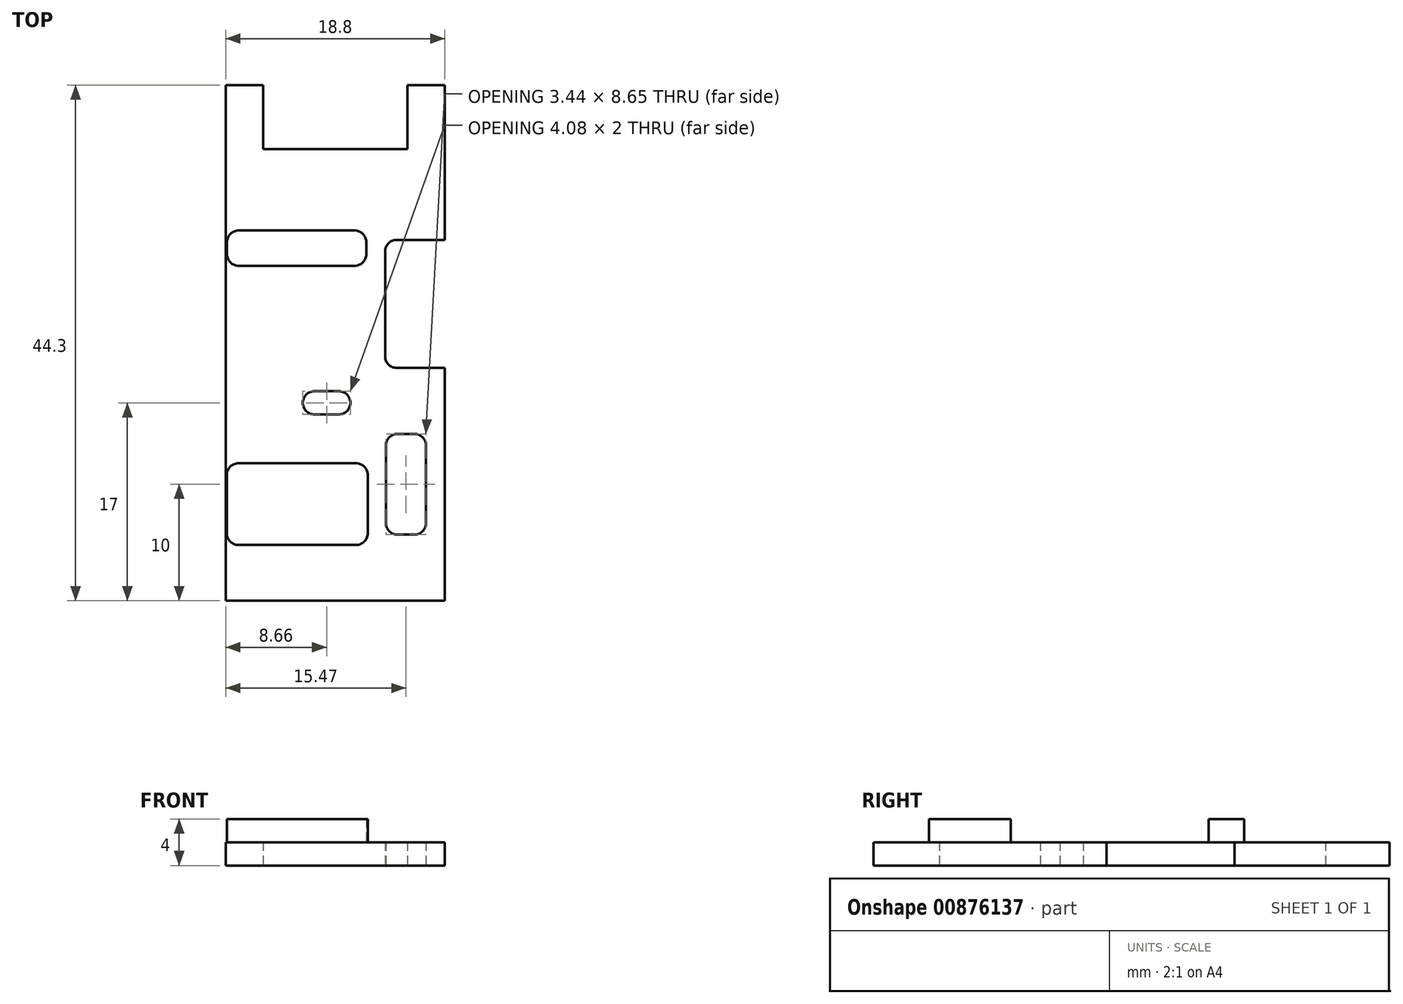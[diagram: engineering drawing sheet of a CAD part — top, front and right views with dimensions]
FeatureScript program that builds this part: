
annotation { "Feature Type Name" : "Feature", "Feature Type Description" : "" }
export const myFeature = defineFeature(function(context is Context, id is Id, definition is map)
    precondition{}
    {
        {
            var Q0;
            Q0=qCreatedBy(makeId("Top.planeOp"),FACE);
            var sketch = newSketch(context, id + "F0", { "sketchPlane" : qUnion([Q0])});
            skLineSegment(sketch, "E0", {"start": v(9.4, 22.15) * mm, "end": v(6.2, 22.15) * mm});
            skLineSegment(sketch, "E1", {"start": v(6.2, 16.65) * mm, "end": v(-6.2, 16.65) * mm});
            skLineSegment(sketch, "E2", {"start": v(-6.2, 22.15) * mm, "end": v(-9.4, 22.15) * mm});
            skLineSegment(sketch, "E3", {"start": v(-9.4, 22.15) * mm, "end": v(-9.4, -22.15) * mm});
            skLineSegment(sketch, "E4", {"start": v(-9.4, -22.15) * mm, "end": v(9.4, -22.15) * mm});
            skLineSegment(sketch, "E5", {"start": v(4.28, -1.15) * mm, "end": v(4.28, 7.85) * mm});
            skPoint(sketch, "E6.visualSharp", {"position": v(4.28, 8.85) * mm});
            skArc(sketch, "E6.filletArc", {"start": v(5.28, 8.85) * mm, "mid": v(4.57, 8.56) * mm, "end": v(4.28, 7.85) * mm});
            skPoint(sketch, "E7.visualSharp", {"position": v(4.28, -2.15) * mm});
            skArc(sketch, "E7.filletArc", {"start": v(4.28, -1.15) * mm, "mid": v(4.57, -1.86) * mm, "end": v(5.28, -2.15) * mm});
            skLineSegment(sketch, "E8.bottom", {"start": v(5.35, -7.82) * mm, "end": v(6.8, -7.82) * mm});
            skLineSegment(sketch, "E8.top", {"start": v(5.35, -16.48) * mm, "end": v(6.8, -16.48) * mm});
            skLineSegment(sketch, "E8.left", {"start": v(4.35, -8.82) * mm, "end": v(4.35, -15.48) * mm});
            skLineSegment(sketch, "E8.right", {"start": v(7.8, -8.82) * mm, "end": v(7.8, -15.48) * mm});
            skLineSegment(sketch, "E9.bottom", {"start": v(-1.78, -4.15) * mm, "end": v(0.3, -4.15) * mm});
            skLineSegment(sketch, "E9.top", {"start": v(-1.78, -6.15) * mm, "end": v(0.3, -6.15) * mm});
            skLineSegment(sketch, "E9.left", {"start": v(-2.78, -5.15) * mm, "end": v(-2.78, -5.15) * mm});
            skLineSegment(sketch, "E9.right", {"start": v(1.3, -5.15) * mm, "end": v(1.3, -5.15) * mm});
            skPoint(sketch, "E10.visualSharp", {"position": v(4.35, -7.82) * mm});
            skArc(sketch, "E10.filletArc", {"start": v(5.35, -7.82) * mm, "mid": v(4.64, -8.12) * mm, "end": v(4.35, -8.82) * mm});
            skPoint(sketch, "E11.visualSharp", {"position": v(7.8, -7.82) * mm});
            skArc(sketch, "E11.filletArc", {"start": v(7.8, -8.82) * mm, "mid": v(7.5, -8.12) * mm, "end": v(6.8, -7.82) * mm});
            skPoint(sketch, "E12.visualSharp", {"position": v(4.35, -16.48) * mm});
            skArc(sketch, "E12.filletArc", {"start": v(4.35, -15.48) * mm, "mid": v(4.64, -16.18) * mm, "end": v(5.35, -16.48) * mm});
            skPoint(sketch, "E13.visualSharp", {"position": v(7.8, -16.48) * mm});
            skArc(sketch, "E13.filletArc", {"start": v(6.8, -16.48) * mm, "mid": v(7.5, -16.18) * mm, "end": v(7.8, -15.48) * mm});
            skPoint(sketch, "E14.visualSharp", {"position": v(-2.78, -4.15) * mm});
            skArc(sketch, "E14.filletArc", {"start": v(-1.78, -4.15) * mm, "mid": v(-2.49, -4.44) * mm, "end": v(-2.78, -5.15) * mm});
            skPoint(sketch, "E15.visualSharp", {"position": v(1.3, -4.15) * mm});
            skArc(sketch, "E15.filletArc", {"start": v(1.3, -5.15) * mm, "mid": v(1, -4.44) * mm, "end": v(0.3, -4.15) * mm});
            skPoint(sketch, "E16.visualSharp", {"position": v(1.3, -6.15) * mm});
            skArc(sketch, "E16.filletArc", {"start": v(0.3, -6.15) * mm, "mid": v(1, -5.86) * mm, "end": v(1.3, -5.15) * mm});
            skPoint(sketch, "E17.visualSharp", {"position": v(-2.78, -6.15) * mm});
            skArc(sketch, "E17.filletArc", {"start": v(-2.78, -5.15) * mm, "mid": v(-2.49, -5.86) * mm, "end": v(-1.78, -6.15) * mm});
            skLineSegment(sketch, "E18", {"start": v(6.07, -19.37) * mm, "end": v(6.07, -7.73) * mm, "construction": true});
            skPoint(sketch, "E18.startSnap0", {"position": v(6.07, -16.48) * mm});
            skPoint(sketch, "E18.endSnap0", {"position": v(6.07, -7.82) * mm});
            skLineSegment(sketch, "E19", {"start": v(3.47, -12.15) * mm, "end": v(8.81, -12.15) * mm, "construction": true});
            skPoint(sketch, "E19.startSnap0", {"position": v(4.35, -12.15) * mm});
            skLineSegment(sketch, "E20", {"start": v(-0.74, -5.47) * mm, "end": v(-0.74, -9.08) * mm, "construction": true});
            skPoint(sketch, "E20.startSnap0", {"position": v(-0.74, -4.15) * mm});
            skLineSegment(sketch, "E21", {"start": v(-3.75, -5.15) * mm, "end": v(2.13, -5.15) * mm, "construction": true});
            skLineSegment(sketch, "E22", {"start": v(-6.2, 22.15) * mm, "end": v(-6.2, 16.65) * mm});
            skLineSegment(sketch, "E23", {"start": v(6.2, 22.15) * mm, "end": v(6.2, 16.65) * mm});
            skLineSegment(sketch, "E24", {"start": v(5.28, 8.85) * mm, "end": v(9.4, 8.85) * mm});
            skLineSegment(sketch, "E25", {"start": v(9.4, 8.85) * mm, "end": v(9.4, 22.15) * mm});
            skLineSegment(sketch, "E26", {"start": v(5.28, -2.15) * mm, "end": v(9.4, -2.15) * mm});
            skLineSegment(sketch, "E27", {"start": v(9.4, -2.15) * mm, "end": v(9.4, -22.15) * mm});
            skSolve(sketch);
        }
        {
            var Q0;
            Q0 = qSketchRegion(id + "F0", true);
            extrude(context, id + "F1", {"entities" : qUnion([Q0]), "depth" : 2 * mm, "offsetDistance" : 25 * mm});
        }
        {
            var Q0;
            Q0=makeQuery(id+"F1.opExtrude","CAP_FACE",FACE,{"disambiguationData":[OSD([sQuery(id+"F0.wireOp",EDGE,"E0"),sQuery(id+"F0.wireOp",EDGE,"vSKlW9BE-0tMY-Gx0d-h0NM-eHRIWNPuGo55"),sQuery(id+"F0.wireOp",EDGE,"E1"),sQuery(id+"F0.wireOp",EDGE,"NluscC6o-Kzi7-0lCj-nFr1-bALU2oggECtv"),sQuery(id+"F0.wireOp",EDGE,"E2"),sQuery(id+"F0.wireOp",EDGE,"E3"),sQuery(id+"F0.wireOp",EDGE,"E4"),sQuery(id+"F0.wireOp",EDGE,"QD9gv3Tt-72UJ-3bKe-3RIz-LiDQutMN64dA"),sQuery(id+"F0.wireOp",EDGE,"9PGKM9NJ-Zi3G-O61R-aaed-Mc24DOAeeQgH"),sQuery(id+"F0.wireOp",EDGE,"E5"),sQuery(id+"F0.wireOp",EDGE,"JoNwm8we-2aQm-wHB8-4yzH-CeIhHuO5SB0L"),sQuery(id+"F0.wireOp",EDGE,"g29vqZCW-IXcO-DqwF-diWq-WlHzeJOLfXhB"),sQuery(id+"F0.wireOp",EDGE,"E6.filletArc"),sQuery(id+"F0.wireOp",EDGE,"E7.filletArc"),sQuery(id+"F0.wireOp",EDGE,"E8.bottom"),sQuery(id+"F0.wireOp",EDGE,"E8.top"),sQuery(id+"F0.wireOp",EDGE,"E8.left"),sQuery(id+"F0.wireOp",EDGE,"E8.right"),sQuery(id+"F0.wireOp",EDGE,"E9.bottom"),sQuery(id+"F0.wireOp",EDGE,"E9.top"),sQuery(id+"F0.wireOp",EDGE,"E10.filletArc"),sQuery(id+"F0.wireOp",EDGE,"E11.filletArc"),sQuery(id+"F0.wireOp",EDGE,"E12.filletArc"),sQuery(id+"F0.wireOp",EDGE,"E13.filletArc"),sQuery(id+"F0.wireOp",EDGE,"E14.filletArc"),sQuery(id+"F0.wireOp",EDGE,"E15.filletArc"),sQuery(id+"F0.wireOp",EDGE,"E16.filletArc"),sQuery(id+"F0.wireOp",EDGE,"E17.filletArc")])],"isStart":false});
            var sketch = newSketch(context, id + "F2", { "sketchPlane" : qUnion([Q0])});
            skLineSegment(sketch, "E28.bottom", {"start": v(-8.29, 9.66) * mm, "end": v(1.66, 9.66) * mm});
            skLineSegment(sketch, "E28.top", {"start": v(-8.29, 6.62) * mm, "end": v(1.66, 6.62) * mm});
            skLineSegment(sketch, "E28.left", {"start": v(-9.29, 8.66) * mm, "end": v(-9.29, 7.62) * mm});
            skLineSegment(sketch, "E28.right", {"start": v(2.66, 8.66) * mm, "end": v(2.66, 7.62) * mm});
            skLineSegment(sketch, "E29.bottom", {"start": v(-8.3, -10.34) * mm, "end": v(1.8, -10.34) * mm});
            skLineSegment(sketch, "E29.top", {"start": v(-8.3, -17.36) * mm, "end": v(1.8, -17.36) * mm});
            skLineSegment(sketch, "E29.left", {"start": v(-9.3, -11.34) * mm, "end": v(-9.3, -16.36) * mm});
            skLineSegment(sketch, "E29.right", {"start": v(2.8, -11.34) * mm, "end": v(2.8, -16.36) * mm});
            skPoint(sketch, "E30.visualSharp", {"position": v(-9.3, -10.34) * mm});
            skArc(sketch, "E30.filletArc", {"start": v(-8.3, -10.34) * mm, "mid": v(-9.01, -10.64) * mm, "end": v(-9.3, -11.34) * mm});
            skPoint(sketch, "E31.visualSharp", {"position": v(-9.3, -17.36) * mm});
            skArc(sketch, "E31.filletArc", {"start": v(-9.3, -16.36) * mm, "mid": v(-9.01, -17.07) * mm, "end": v(-8.3, -17.36) * mm});
            skPoint(sketch, "E32.visualSharp", {"position": v(2.8, -17.36) * mm});
            skArc(sketch, "E32.filletArc", {"start": v(1.8, -17.36) * mm, "mid": v(2.5, -17.07) * mm, "end": v(2.8, -16.36) * mm});
            skPoint(sketch, "E33.visualSharp", {"position": v(2.8, -10.34) * mm});
            skArc(sketch, "E33.filletArc", {"start": v(2.8, -11.34) * mm, "mid": v(2.5, -10.64) * mm, "end": v(1.8, -10.34) * mm});
            skPoint(sketch, "E34.visualSharp", {"position": v(-9.29, 9.66) * mm});
            skArc(sketch, "E34.filletArc", {"start": v(-8.29, 9.66) * mm, "mid": v(-9, 9.37) * mm, "end": v(-9.29, 8.66) * mm});
            skPoint(sketch, "E35.visualSharp", {"position": v(-9.29, 6.62) * mm});
            skArc(sketch, "E35.filletArc", {"start": v(-9.29, 7.62) * mm, "mid": v(-9, 6.91) * mm, "end": v(-8.29, 6.62) * mm});
            skPoint(sketch, "E36.visualSharp", {"position": v(2.66, 6.62) * mm});
            skArc(sketch, "E36.filletArc", {"start": v(1.66, 6.62) * mm, "mid": v(2.37, 6.91) * mm, "end": v(2.66, 7.62) * mm});
            skPoint(sketch, "E37.visualSharp", {"position": v(2.66, 9.66) * mm});
            skArc(sketch, "E37.filletArc", {"start": v(2.66, 8.66) * mm, "mid": v(2.37, 9.37) * mm, "end": v(1.66, 9.66) * mm});
            skLineSegment(sketch, "E38", {"start": v(-10.26, -13.85) * mm, "end": v(3.48, -13.85) * mm, "construction": true});
            skPoint(sketch, "E38.startSnap0", {"position": v(-9.3, -13.85) * mm});
            skLineSegment(sketch, "E39", {"start": v(-3.26, -9.25) * mm, "end": v(-3.26, -18.2) * mm, "construction": true});
            skPoint(sketch, "E39.startSnap0", {"position": v(-3.26, -10.34) * mm});
            skLineSegment(sketch, "E40", {"start": v(-10.28, 8.14) * mm, "end": v(3.34, 8.14) * mm, "construction": true});
            skPoint(sketch, "E40.startSnap0", {"position": v(-9.29, 8.14) * mm});
            skLineSegment(sketch, "E41", {"start": v(-3.31, 5.86) * mm, "end": v(-3.31, 10.61) * mm, "construction": true});
            skPoint(sketch, "E41.startSnap0", {"position": v(-3.31, 6.62) * mm});
            skSolve(sketch);
        }
        {
            var Q0;
            Q0 = qSketchRegion(id + "F2", true);
            extrude(context, id + "F3", {"entities" : qUnion([Q0]), "operationType" : NewBodyOperationType.ADD, "depth" : 2 * mm, "offsetDistance" : 25 * mm});
        }
    });
